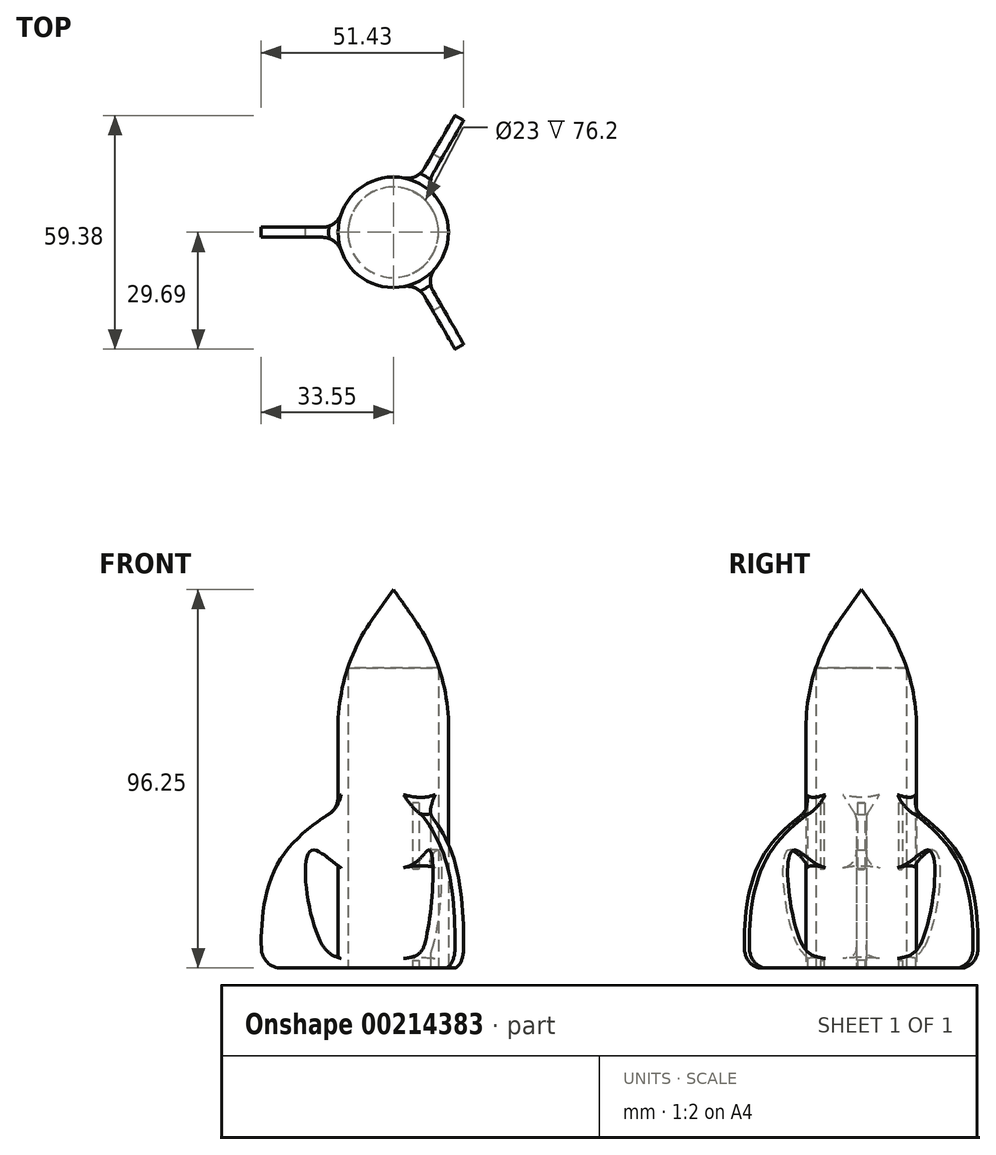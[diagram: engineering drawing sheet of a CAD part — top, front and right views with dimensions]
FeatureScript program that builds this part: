
annotation { "Feature Type Name" : "Feature", "Feature Type Description" : "" }
export const myFeature = defineFeature(function(context is Context, id is Id, definition is map)
    precondition{}
    {
        {
            var Q0;
            Q0=qCreatedBy(makeId("Top.planeOp"),FACE);
            var sketch = newSketch(context, id + "F0", { "sketchPlane" : qUnion([Q0])});
            skCircle(sketch, "E0", {"center": v(0, 0) * mm, "radius": 11.5 * mm});
            skCircle(sketch, "E1", {"center": v(0, 0) * mm, "radius": 14.04 * mm});
            skSolve(sketch);
        }
        {
            var Q0;
            Q0=makeQuery(id+"F0.imprint","IMPRINT",FACE,{"disambiguationData":[TD([[makeQuery(id+"F0.imprint","IMPRINT",EDGE,{"derivedFrom":sQuery(id+"F0.wireOp",EDGE,"E0")}),-1.0]])]});
            extrude(context, id + "F1", {"entities" : qUnion([Q0]), "depth" : 76.2 * mm});
        }
        {
            var Q0;
            Q0=qCreatedBy(makeId("Top.planeOp"),FACE);
            cPlane(context, id + "F2", {"entities" : qUnion([Q0]), "cplaneType" : CPlaneType.OFFSET, "offset" : 76.2 * mm, "width" : 152.4 * mm, "height" : 152.4 * mm});
        }
        {
            var Q0;
            Q0=qCreatedBy(id+"F2.planeOp",FACE);
            var sketch = newSketch(context, id + "F3", { "sketchPlane" : qUnion([Q0])});
            skCircle(sketch, "E2.0", {"center": v(0, 0) * mm, "radius": 14.04 * mm});
            skSolve(sketch);
        }
        {
            var Q0;
            Q0=qSketchRegion(id+"F3",true);
            extrude(context, id + "F4", {"entities" : qUnion([Q0]), "operationType" : NewBodyOperationType.ADD, "depth" : 25.4 * mm, "hasDraft" : true, "draftAngle" : 35 * degree, "draftPullDirection" : true});
        }
        {
            var Q0;
            Q0=makeQuery(id+"F4.opExtrude","SWEPT_FACE",FACE,{"disambiguationData":[OSD([sQuery(id+"F3.wireOp",EDGE,"E2.0")])]});
            fillet(context, id + "F5", {"entities" : qUnion([Q0]), "radius" : 48.26 * mm, "tangentPropagation" : true, "allowEdgeOverflow" : false});
        }
        {
            var Q0;
            Q0=qCreatedBy(makeId("Front.planeOp"),FACE);
            var sketch = newSketch(context, id + "F6", { "sketchPlane" : qUnion([Q0])});
            skFitSpline(sketch, "E3", {"points": [v(-11.46, 41.94) * mm, v(-29.4, 26.34) * mm, v(-33.2, 0) * mm], "startDerivative": vector(-21.33, -11.42) * mm, "endDerivative": vector(2.93, -26.57) * mm});
            skLineSegment(sketch, "E4", {"start": v(-11.46, 41.94) * mm, "end": v(-11.46, 25.14) * mm});
            skFitSpline(sketch, "E5", {"points": [v(-11.46, 25.14) * mm, v(-20.59, 29.95) * mm, v(-18, 5.87) * mm, v(-11.46, 1.95) * mm], "startDerivative": vector(-19.43, -9.54) * mm, "endDerivative": vector(23.3, -8.7) * mm});
            skLineSegment(sketch, "E6", {"start": v(-11.46, 0) * mm, "end": v(-11.46, 1.95) * mm});
            skLineSegment(sketch, "E7", {"start": v(-33.2, 0) * mm, "end": v(-11.46, 0) * mm});
            skSolve(sketch);
        }
        {
            var Q0;
            Q0=makeQuery(id+"F6.imprint","IMPRINT",FACE,{"disambiguationData":[TD([[makeQuery(id+"F6.imprint","IMPRINT",EDGE,{"derivedFrom":sQuery(id+"F6.wireOp",EDGE,"E3")}),1.0]])]});
            extrude(context, id + "F7", {"entities" : qUnion([Q0]), "oppositeDirection" : true, "depth" : 1.27 * mm, "hasSecondDirection" : true, "secondDirectionOppositeDirection" : false, "secondDirectionDepth" : 1.27 * mm});
        }
        {
            var Q0;
            Q0=makeQuery(id+"F7.opExtrude","SWEPT_BODY",BODY,{"disambiguationData":[OSD([sQuery(id+"F6.wireOp",EDGE,"E3"),sQuery(id+"F6.wireOp",EDGE,"E4"),sQuery(id+"F6.wireOp",EDGE,"E5"),sQuery(id+"F6.wireOp",EDGE,"E6"),sQuery(id+"F6.wireOp",EDGE,"E7")])]});
            var Q1;
            Q1=makeQuery(id+"F1.opExtrude","CAP_EDGE",EDGE,{"disambiguationData":[OSD([sQuery(id+"F0.wireOp",EDGE,"E0")])],"isStart":true});
            circularPattern(context, id + "F8", {"entities" : qUnion([Q0]), "axis" : qUnion([Q1]), "angle" : 360 * degree, "instanceCount" : 3, "equalSpace" : true});
        }
        {
            var Q0;
            Q0=makeQuery(id+"F7.opExtrude","SWEPT_BODY",BODY,{"disambiguationData":[OSD([sQuery(id+"F6.wireOp",EDGE,"E3"),sQuery(id+"F6.wireOp",EDGE,"E4"),sQuery(id+"F6.wireOp",EDGE,"E5"),sQuery(id+"F6.wireOp",EDGE,"E6"),sQuery(id+"F6.wireOp",EDGE,"E7")])]});
            var Q1;
            Q1=makeQuery(id+"F8.opPattern","COPY",BODY,{"derivedFrom":makeQuery(id+"F7.opExtrude","SWEPT_BODY",BODY,{"disambiguationData":[OSD([sQuery(id+"F6.wireOp",EDGE,"E3"),sQuery(id+"F6.wireOp",EDGE,"E4"),sQuery(id+"F6.wireOp",EDGE,"E5"),sQuery(id+"F6.wireOp",EDGE,"E6"),sQuery(id+"F6.wireOp",EDGE,"E7")])]}),"instanceName":"1"});
            var Q2;
            Q2=makeQuery(id+"F1.opExtrude","SWEPT_BODY",BODY,{"disambiguationData":[OSD([sQuery(id+"F0.wireOp",EDGE,"E0"),sQuery(id+"F0.wireOp",EDGE,"E1")])]});
            var Q3;
            Q3=makeQuery(id+"F8.opPattern","COPY",BODY,{"derivedFrom":makeQuery(id+"F7.opExtrude","SWEPT_BODY",BODY,{"disambiguationData":[OSD([sQuery(id+"F6.wireOp",EDGE,"E3"),sQuery(id+"F6.wireOp",EDGE,"E4"),sQuery(id+"F6.wireOp",EDGE,"E5"),sQuery(id+"F6.wireOp",EDGE,"E6"),sQuery(id+"F6.wireOp",EDGE,"E7")])]}),"instanceName":"2"});
            booleanBodies(context, id + "F9", {"operationType" : BooleanOperationType.UNION, "tools" : qUnion([Q0, Q1, Q2, Q3])});
        }
        {
            var Q0;
            Q0=makeQuery(id+"F9.opBoolean","INTERSECT",EDGE,{"disambiguationData":[OD(1.0)],"derivedFrom":[makeQuery(id+"F1.opExtrude","SWEPT_FACE",FACE,{"disambiguationData":[OSD([sQuery(id+"F0.wireOp",EDGE,"E1")])]}),makeQuery(id+"F8.opPattern","COPY",FACE,{"derivedFrom":makeQuery(id+"F7.opExtrude","CAP_FACE",FACE,{"disambiguationData":[OSD([sQuery(id+"F6.wireOp",EDGE,"E3"),sQuery(id+"F6.wireOp",EDGE,"E4"),sQuery(id+"F6.wireOp",EDGE,"E5"),sQuery(id+"F6.wireOp",EDGE,"E6"),sQuery(id+"F6.wireOp",EDGE,"E7")])],"isStart":true}),"instanceName":"1"})]});
            var Q1;
            Q1=makeQuery(id+"F9.opBoolean","INTERSECT",EDGE,{"disambiguationData":[OD(0.0)],"derivedFrom":[makeQuery(id+"F1.opExtrude","SWEPT_FACE",FACE,{"disambiguationData":[OSD([sQuery(id+"F0.wireOp",EDGE,"E1")])]}),makeQuery(id+"F8.opPattern","COPY",FACE,{"derivedFrom":makeQuery(id+"F7.opExtrude","CAP_FACE",FACE,{"disambiguationData":[OSD([sQuery(id+"F6.wireOp",EDGE,"E3"),sQuery(id+"F6.wireOp",EDGE,"E4"),sQuery(id+"F6.wireOp",EDGE,"E5"),sQuery(id+"F6.wireOp",EDGE,"E6"),sQuery(id+"F6.wireOp",EDGE,"E7")])],"isStart":true}),"instanceName":"1"})]});
            var Q2;
            Q2=makeQuery(id+"F9.opBoolean","INTERSECT",EDGE,{"disambiguationData":[OD(1.0)],"derivedFrom":[makeQuery(id+"F1.opExtrude","SWEPT_FACE",FACE,{"disambiguationData":[OSD([sQuery(id+"F0.wireOp",EDGE,"E1")])]}),makeQuery(id+"F8.opPattern","COPY",FACE,{"derivedFrom":makeQuery(id+"F7.opExtrude","CAP_FACE",FACE,{"disambiguationData":[OSD([sQuery(id+"F6.wireOp",EDGE,"E3"),sQuery(id+"F6.wireOp",EDGE,"E4"),sQuery(id+"F6.wireOp",EDGE,"E5"),sQuery(id+"F6.wireOp",EDGE,"E6"),sQuery(id+"F6.wireOp",EDGE,"E7")])],"isStart":false}),"instanceName":"2"})]});
            var Q3;
            Q3=makeQuery(id+"F9.opBoolean","INTERSECT",EDGE,{"disambiguationData":[OD(0.0)],"derivedFrom":[makeQuery(id+"F1.opExtrude","SWEPT_FACE",FACE,{"disambiguationData":[OSD([sQuery(id+"F0.wireOp",EDGE,"E1")])]}),makeQuery(id+"F8.opPattern","COPY",FACE,{"derivedFrom":makeQuery(id+"F7.opExtrude","CAP_FACE",FACE,{"disambiguationData":[OSD([sQuery(id+"F6.wireOp",EDGE,"E3"),sQuery(id+"F6.wireOp",EDGE,"E4"),sQuery(id+"F6.wireOp",EDGE,"E5"),sQuery(id+"F6.wireOp",EDGE,"E6"),sQuery(id+"F6.wireOp",EDGE,"E7")])],"isStart":false}),"instanceName":"2"})]});
            var Q4;
            Q4=makeQuery(id+"F9.opBoolean","INTERSECT",EDGE,{"disambiguationData":[OD(1.0)],"derivedFrom":[makeQuery(id+"F1.opExtrude","SWEPT_FACE",FACE,{"disambiguationData":[OSD([sQuery(id+"F0.wireOp",EDGE,"E1")])]}),makeQuery(id+"F8.opPattern","COPY",FACE,{"derivedFrom":makeQuery(id+"F7.opExtrude","CAP_FACE",FACE,{"disambiguationData":[OSD([sQuery(id+"F6.wireOp",EDGE,"E3"),sQuery(id+"F6.wireOp",EDGE,"E4"),sQuery(id+"F6.wireOp",EDGE,"E5"),sQuery(id+"F6.wireOp",EDGE,"E6"),sQuery(id+"F6.wireOp",EDGE,"E7")])],"isStart":false}),"instanceName":"1"})]});
            var Q5;
            Q5=makeQuery(id+"F9.opBoolean","INTERSECT",EDGE,{"disambiguationData":[OD(0.0)],"derivedFrom":[makeQuery(id+"F1.opExtrude","SWEPT_FACE",FACE,{"disambiguationData":[OSD([sQuery(id+"F0.wireOp",EDGE,"E1")])]}),makeQuery(id+"F8.opPattern","COPY",FACE,{"derivedFrom":makeQuery(id+"F7.opExtrude","CAP_FACE",FACE,{"disambiguationData":[OSD([sQuery(id+"F6.wireOp",EDGE,"E3"),sQuery(id+"F6.wireOp",EDGE,"E4"),sQuery(id+"F6.wireOp",EDGE,"E5"),sQuery(id+"F6.wireOp",EDGE,"E6"),sQuery(id+"F6.wireOp",EDGE,"E7")])],"isStart":false}),"instanceName":"1"})]});
            var Q6;
            Q6=makeQuery(id+"F9.opBoolean","INTERSECT",EDGE,{"disambiguationData":[OD(1.0)],"derivedFrom":[makeQuery(id+"F1.opExtrude","SWEPT_FACE",FACE,{"disambiguationData":[OSD([sQuery(id+"F0.wireOp",EDGE,"E1")])]}),makeQuery(id+"F8.opPattern","COPY",FACE,{"derivedFrom":makeQuery(id+"F7.opExtrude","CAP_FACE",FACE,{"disambiguationData":[OSD([sQuery(id+"F6.wireOp",EDGE,"E3"),sQuery(id+"F6.wireOp",EDGE,"E4"),sQuery(id+"F6.wireOp",EDGE,"E5"),sQuery(id+"F6.wireOp",EDGE,"E6"),sQuery(id+"F6.wireOp",EDGE,"E7")])],"isStart":true}),"instanceName":"2"})]});
            var Q7;
            Q7=makeQuery(id+"F9.opBoolean","INTERSECT",EDGE,{"disambiguationData":[OD(0.0)],"derivedFrom":[makeQuery(id+"F1.opExtrude","SWEPT_FACE",FACE,{"disambiguationData":[OSD([sQuery(id+"F0.wireOp",EDGE,"E1")])]}),makeQuery(id+"F8.opPattern","COPY",FACE,{"derivedFrom":makeQuery(id+"F7.opExtrude","CAP_FACE",FACE,{"disambiguationData":[OSD([sQuery(id+"F6.wireOp",EDGE,"E3"),sQuery(id+"F6.wireOp",EDGE,"E4"),sQuery(id+"F6.wireOp",EDGE,"E5"),sQuery(id+"F6.wireOp",EDGE,"E6"),sQuery(id+"F6.wireOp",EDGE,"E7")])],"isStart":true}),"instanceName":"2"})]});
            var Q8;
            Q8=makeQuery(id+"F9.opBoolean","INTERSECT",EDGE,{"disambiguationData":[OD(1.0)],"derivedFrom":[makeQuery(id+"F1.opExtrude","SWEPT_FACE",FACE,{"disambiguationData":[OSD([sQuery(id+"F0.wireOp",EDGE,"E1")])]}),makeQuery(id+"F7.opExtrude","CAP_FACE",FACE,{"disambiguationData":[OSD([sQuery(id+"F6.wireOp",EDGE,"E3"),sQuery(id+"F6.wireOp",EDGE,"E4"),sQuery(id+"F6.wireOp",EDGE,"E5"),sQuery(id+"F6.wireOp",EDGE,"E6"),sQuery(id+"F6.wireOp",EDGE,"E7")])],"isStart":false})]});
            var Q9;
            Q9=makeQuery(id+"F9.opBoolean","INTERSECT",EDGE,{"disambiguationData":[OD(0.0)],"derivedFrom":[makeQuery(id+"F1.opExtrude","SWEPT_FACE",FACE,{"disambiguationData":[OSD([sQuery(id+"F0.wireOp",EDGE,"E1")])]}),makeQuery(id+"F7.opExtrude","CAP_FACE",FACE,{"disambiguationData":[OSD([sQuery(id+"F6.wireOp",EDGE,"E3"),sQuery(id+"F6.wireOp",EDGE,"E4"),sQuery(id+"F6.wireOp",EDGE,"E5"),sQuery(id+"F6.wireOp",EDGE,"E6"),sQuery(id+"F6.wireOp",EDGE,"E7")])],"isStart":false})]});
            var Q10;
            Q10=makeQuery(id+"F9.opBoolean","INTERSECT",EDGE,{"disambiguationData":[OD(1.0)],"derivedFrom":[makeQuery(id+"F1.opExtrude","SWEPT_FACE",FACE,{"disambiguationData":[OSD([sQuery(id+"F0.wireOp",EDGE,"E1")])]}),makeQuery(id+"F7.opExtrude","CAP_FACE",FACE,{"disambiguationData":[OSD([sQuery(id+"F6.wireOp",EDGE,"E3"),sQuery(id+"F6.wireOp",EDGE,"E4"),sQuery(id+"F6.wireOp",EDGE,"E5"),sQuery(id+"F6.wireOp",EDGE,"E6"),sQuery(id+"F6.wireOp",EDGE,"E7")])],"isStart":true})]});
            var Q11;
            Q11=makeQuery(id+"F9.opBoolean","INTERSECT",EDGE,{"disambiguationData":[OD(0.0)],"derivedFrom":[makeQuery(id+"F1.opExtrude","SWEPT_FACE",FACE,{"disambiguationData":[OSD([sQuery(id+"F0.wireOp",EDGE,"E1")])]}),makeQuery(id+"F7.opExtrude","CAP_FACE",FACE,{"disambiguationData":[OSD([sQuery(id+"F6.wireOp",EDGE,"E3"),sQuery(id+"F6.wireOp",EDGE,"E4"),sQuery(id+"F6.wireOp",EDGE,"E5"),sQuery(id+"F6.wireOp",EDGE,"E6"),sQuery(id+"F6.wireOp",EDGE,"E7")])],"isStart":true})]});
            fillet(context, id + "F10", {"entities" : qUnion([Q0, Q1, Q2, Q3, Q4, Q5, Q6, Q7, Q8, Q9, Q10, Q11]), "radius" : 5.08 * mm, "tangentPropagation" : true, "allowEdgeOverflow" : false});
        }
        {
            var Q0;
            Q0=makeQuery(id+"F9.opBoolean","INTERSECT",EDGE,{"derivedFrom":[makeQuery(id+"F1.opExtrude","SWEPT_FACE",FACE,{"disambiguationData":[OSD([sQuery(id+"F0.wireOp",EDGE,"E1")])]}),makeQuery(id+"F7.opExtrude","SWEPT_FACE",FACE,{"disambiguationData":[OSD([sQuery(id+"F6.wireOp",EDGE,"E3")])]})]});
            var Q1;
            Q1=makeQuery(id+"F9.opBoolean","INTERSECT",EDGE,{"derivedFrom":[makeQuery(id+"F1.opExtrude","SWEPT_FACE",FACE,{"disambiguationData":[OSD([sQuery(id+"F0.wireOp",EDGE,"E1")])]}),makeQuery(id+"F8.opPattern","COPY",FACE,{"derivedFrom":makeQuery(id+"F7.opExtrude","SWEPT_FACE",FACE,{"disambiguationData":[OSD([sQuery(id+"F6.wireOp",EDGE,"E3")])]}),"instanceName":"1"})]});
            var Q2;
            Q2=makeQuery(id+"F9.opBoolean","INTERSECT",EDGE,{"derivedFrom":[makeQuery(id+"F1.opExtrude","SWEPT_FACE",FACE,{"disambiguationData":[OSD([sQuery(id+"F0.wireOp",EDGE,"E1")])]}),makeQuery(id+"F8.opPattern","COPY",FACE,{"derivedFrom":makeQuery(id+"F7.opExtrude","SWEPT_FACE",FACE,{"disambiguationData":[OSD([sQuery(id+"F6.wireOp",EDGE,"E3")])]}),"instanceName":"2"})]});
            fillet(context, id + "F11", {"entities" : qUnion([Q0, Q1, Q2]), "radius" : 5.08 * mm, "tangentPropagation" : true, "allowEdgeOverflow" : false});
        }
        {
            var Q0;
            Q0=makeQuery(id+"F7.opExtrude","SWEPT_EDGE",EDGE,{"disambiguationData":[OSD([sQuery(id+"F6.wireOp",EDGE,"E3"),sQuery(id+"F6.wireOp",EDGE,"E7")])]});
            var Q1;
            Q1=makeQuery(id+"F8.opPattern","COPY",EDGE,{"derivedFrom":makeQuery(id+"F7.opExtrude","SWEPT_EDGE",EDGE,{"disambiguationData":[OSD([sQuery(id+"F6.wireOp",EDGE,"E3"),sQuery(id+"F6.wireOp",EDGE,"E7")])]}),"instanceName":"2"});
            var Q2;
            Q2=makeQuery(id+"F8.opPattern","COPY",EDGE,{"derivedFrom":makeQuery(id+"F7.opExtrude","SWEPT_EDGE",EDGE,{"disambiguationData":[OSD([sQuery(id+"F6.wireOp",EDGE,"E3"),sQuery(id+"F6.wireOp",EDGE,"E7")])]}),"instanceName":"1"});
            fillet(context, id + "F12", {"entities" : qUnion([Q0, Q1, Q2]), "radius" : 5.08 * mm, "tangentPropagation" : true, "allowEdgeOverflow" : false});
        }
    });
